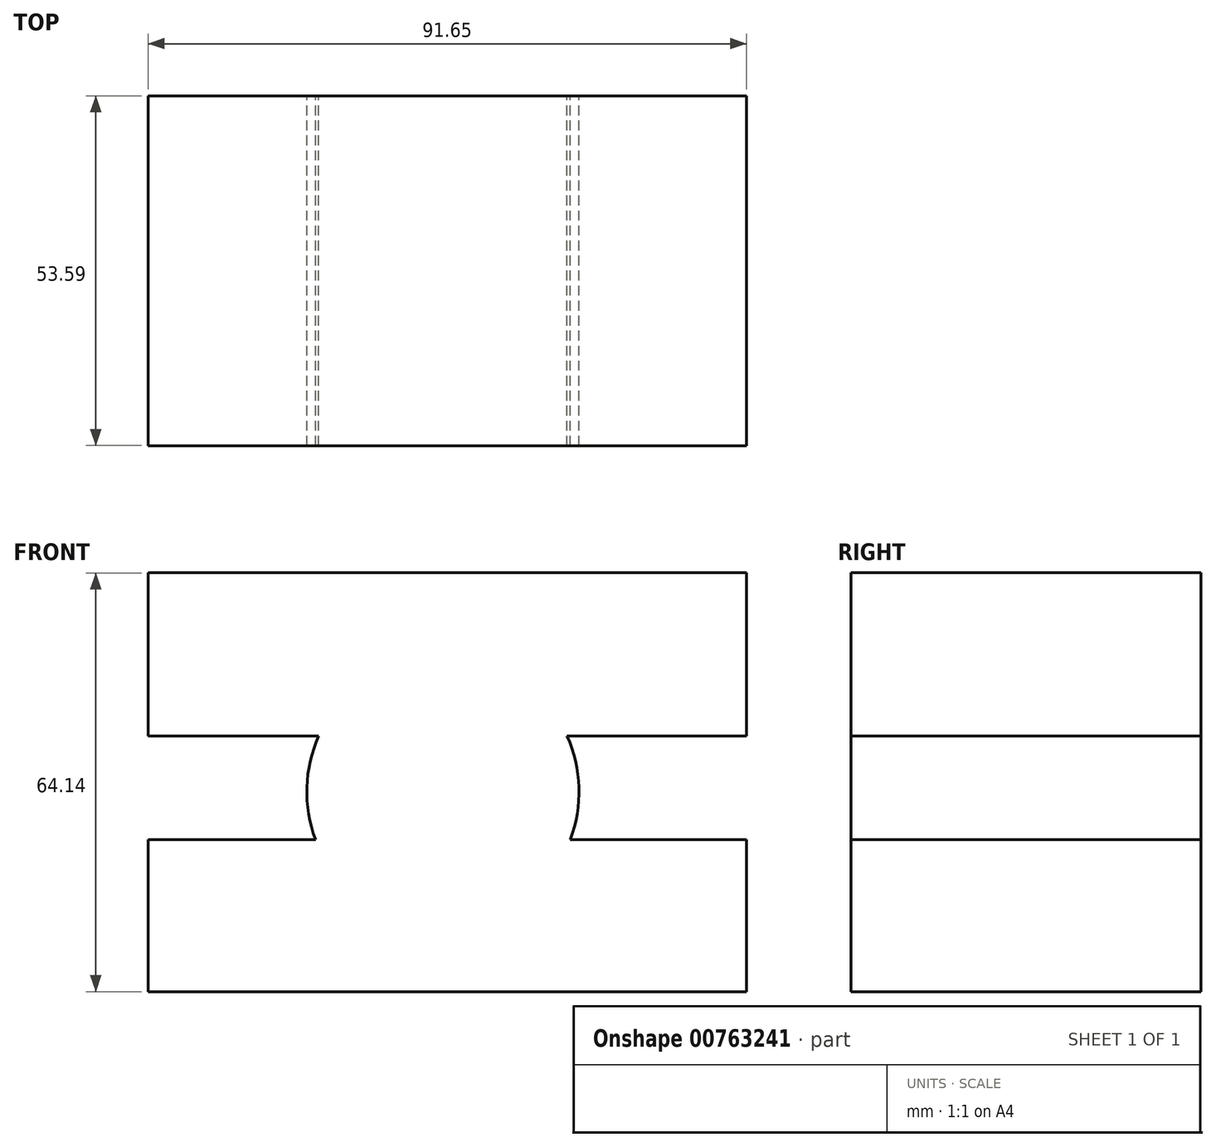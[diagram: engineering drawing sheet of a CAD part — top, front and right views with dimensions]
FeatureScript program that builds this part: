
annotation { "Feature Type Name" : "Feature", "Feature Type Description" : "" }
export const myFeature = defineFeature(function(context is Context, id is Id, definition is map)
    precondition{}
    {
        {
            var Q0;
            Q0=qCreatedBy(makeId("Front.planeOp"),FACE);
            var sketch = newSketch(context, id + "F0", { "sketchPlane" : qUnion([Q0])});
            skLineSegment(sketch, "E0.bottom", {"start": v(-45.16, 33.52) * mm, "end": v(46.49, 33.52) * mm});
            skLineSegment(sketch, "E0.top", {"start": v(-45.16, -30.62) * mm, "end": v(46.49, -30.62) * mm});
            skLineSegment(sketch, "E0.left", {"start": v(-45.16, 33.52) * mm, "end": v(-45.16, -30.62) * mm});
            skLineSegment(sketch, "E0.right", {"start": v(46.49, 33.52) * mm, "end": v(46.49, -30.62) * mm});
            skCircle(sketch, "E1", {"center": v(0, 0) * mm, "radius": 20.84 * mm});
            skLineSegment(sketch, "E2", {"start": v(-45.16, 8.53) * mm, "end": v(-19.02, 8.53) * mm});
            skLineSegment(sketch, "E3", {"start": v(-45.16, -7.34) * mm, "end": v(-19.5, -7.34) * mm});
            skLineSegment(sketch, "E4", {"start": v(19.02, 8.53) * mm, "end": v(46.49, 8.53) * mm});
            skLineSegment(sketch, "E5", {"start": v(19.5, -7.34) * mm, "end": v(46.49, -7.34) * mm});
            skSolve(sketch);
        }
        {
            var Q0;
            {var subQ4=sQuery(id+"F0.wireOp",EDGE,"E0.top");Q0=makeQuery(id+"F0.imprint","IMPRINT",FACE,{"disambiguationData":[TD([[makeQuery(id+"F0.imprint","IMPRINT",EDGE,{"derivedFrom":subQ4}),1.0]])]});}
            var Q1;
            {var subQ4=sQuery(id+"F0.wireOp",EDGE,"E0.bottom");Q1=makeQuery(id+"F0.imprint","IMPRINT",FACE,{"disambiguationData":[TD([[makeQuery(id+"F0.imprint","IMPRINT",EDGE,{"derivedFrom":subQ4}),-1.0]])]});}
            var Q2;
            {var subQ0=sQuery(id+"F0.wireOp",EDGE,"E1");var subQ1=makeQuery(id+"F0.imprint","INTERSECT",VERTEX,{"derivedFrom":[subQ0,sQuery(id+"F0.wireOp",EDGE,"E2")]});Q2=makeQuery(id+"F0.imprint","IMPRINT",FACE,{"disambiguationData":[TD([[makeQuery(id+"F0.imprint","IMPRINT",EDGE,{"disambiguationData":[TD([[subQ1,1.0]])],"derivedFrom":subQ0}),1.0]])]});}
            extrude(context, id + "F1", {"entities" : qUnion([Q0, Q1, Q2]), "depth" : 53.6 * mm, "offsetDistance" : 25.4 * mm});
        }
    });
